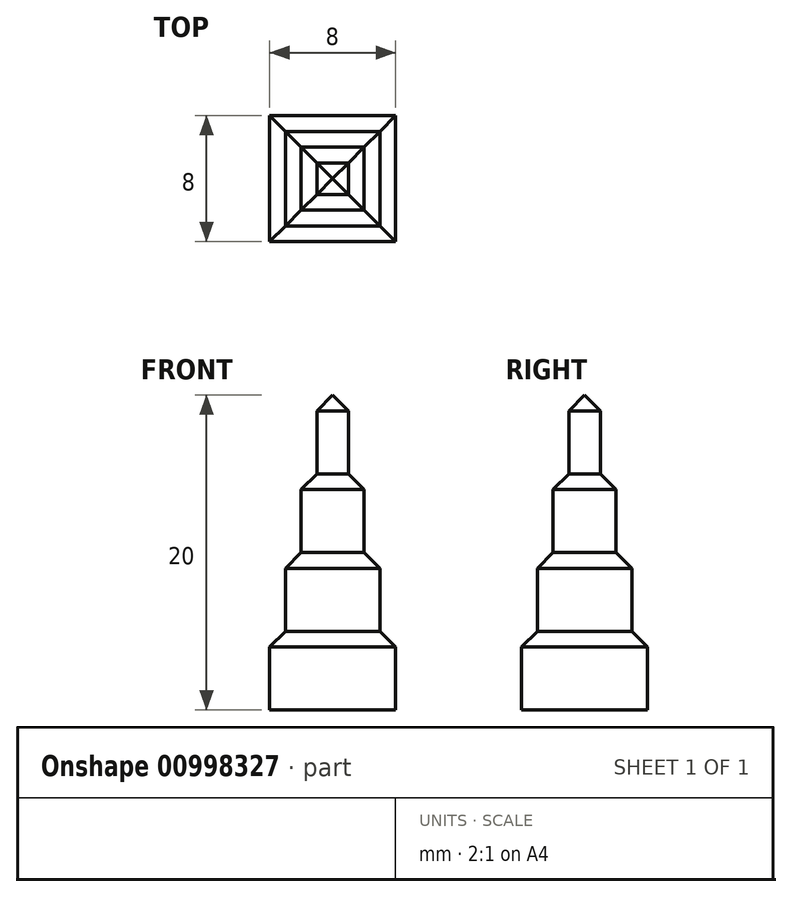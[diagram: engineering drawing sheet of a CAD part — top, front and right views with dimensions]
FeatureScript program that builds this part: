
annotation { "Feature Type Name" : "Feature", "Feature Type Description" : "" }
export const myFeature = defineFeature(function(context is Context, id is Id, definition is map)
    precondition{}
    {
        {
            var Q0;
            Q0=qCreatedBy(makeId("Top.planeOp"),FACE);
            var sketch = newSketch(context, id + "F0", { "sketchPlane" : qUnion([Q0])});
            skLineSegment(sketch, "E0.bottom", {"start": v(1, 1) * mm, "end": v(-1, 1) * mm});
            skLineSegment(sketch, "E0.top", {"start": v(1, -1) * mm, "end": v(-1, -1) * mm});
            skLineSegment(sketch, "E0.left", {"start": v(1, 1) * mm, "end": v(1, -1) * mm});
            skLineSegment(sketch, "E0.right", {"start": v(-1, 1) * mm, "end": v(-1, -1) * mm});
            skPoint(sketch, "E0.middle", {"position": v(0, 0) * mm});
            skLineSegment(sketch, "E1.bottom", {"start": v(2, 2) * mm, "end": v(-2, 2) * mm});
            skLineSegment(sketch, "E1.top", {"start": v(2, -2) * mm, "end": v(-2, -2) * mm});
            skLineSegment(sketch, "E1.left", {"start": v(2, 2) * mm, "end": v(2, -2) * mm});
            skLineSegment(sketch, "E1.right", {"start": v(-2, 2) * mm, "end": v(-2, -2) * mm});
            skLineSegment(sketch, "E2.bottom", {"start": v(3, 3) * mm, "end": v(-3, 3) * mm});
            skLineSegment(sketch, "E2.top", {"start": v(3, -3) * mm, "end": v(-3, -3) * mm});
            skLineSegment(sketch, "E2.left", {"start": v(3, 3) * mm, "end": v(3, -3) * mm});
            skLineSegment(sketch, "E2.right", {"start": v(-3, 3) * mm, "end": v(-3, -3) * mm});
            skLineSegment(sketch, "E3.bottom", {"start": v(4, 4) * mm, "end": v(-4, 4) * mm});
            skLineSegment(sketch, "E3.top", {"start": v(4, -4) * mm, "end": v(-4, -4) * mm});
            skLineSegment(sketch, "E3.left", {"start": v(4, 4) * mm, "end": v(4, -4) * mm});
            skLineSegment(sketch, "E3.right", {"start": v(-4, 4) * mm, "end": v(-4, -4) * mm});
            skSolve(sketch);
        }
        {
            var Q0;
            Q0=makeQuery(id+"F0.imprint","IMPRINT",FACE,{"disambiguationData":[TD([[makeQuery(id+"F0.imprint","IMPRINT",EDGE,{"derivedFrom":sQuery(id+"F0.wireOp",EDGE,"E2.bottom")}),-1.0]])]});
            extrude(context, id + "F1", {"entities" : qUnion([Q0]), "depth" : 5 * mm, "offsetDistance" : 25 * mm});
        }
        {
            var Q0;
            Q0=makeQuery(id+"F0.imprint","IMPRINT",FACE,{"disambiguationData":[TD([[makeQuery(id+"F0.imprint","IMPRINT",EDGE,{"derivedFrom":sQuery(id+"F0.wireOp",EDGE,"E1.bottom")}),-1.0]])]});
            extrude(context, id + "F2", {"entities" : qUnion([Q0]), "operationType" : NewBodyOperationType.ADD, "depth" : 10 * mm, "offsetDistance" : 25 * mm});
        }
        {
            var Q0;
            Q0=makeQuery(id+"F0.imprint","IMPRINT",FACE,{"disambiguationData":[TD([[makeQuery(id+"F0.imprint","IMPRINT",EDGE,{"derivedFrom":sQuery(id+"F0.wireOp",EDGE,"E0.bottom")}),-1.0]])]});
            extrude(context, id + "F3", {"entities" : qUnion([Q0]), "operationType" : NewBodyOperationType.ADD, "depth" : 15 * mm, "offsetDistance" : 25 * mm});
        }
        {
            var Q0;
            Q0=makeQuery(id+"F0.imprint","IMPRINT",FACE,{"disambiguationData":[TD([[makeQuery(id+"F0.imprint","IMPRINT",EDGE,{"derivedFrom":sQuery(id+"F0.wireOp",EDGE,"E0.bottom")}),1.0]])]});
            extrude(context, id + "F4", {"entities" : qUnion([Q0]), "operationType" : NewBodyOperationType.ADD, "depth" : 20 * mm, "offsetDistance" : 25 * mm});
        }
        {
            var Q0;
            Q0=makeQuery(id+"F1.opExtrude","CAP_EDGE",EDGE,{"disambiguationData":[OSD([sQuery(id+"F0.wireOp",EDGE,"E3.top")])],"isStart":false});
            var Q1;
            Q1=makeQuery(id+"F1.opExtrude","CAP_EDGE",EDGE,{"disambiguationData":[OSD([sQuery(id+"F0.wireOp",EDGE,"E3.left")])],"isStart":false});
            var Q2;
            Q2=makeQuery(id+"F1.opExtrude","CAP_EDGE",EDGE,{"disambiguationData":[OSD([sQuery(id+"F0.wireOp",EDGE,"E3.bottom")])],"isStart":false});
            var Q3;
            Q3=makeQuery(id+"F1.opExtrude","CAP_EDGE",EDGE,{"disambiguationData":[OSD([sQuery(id+"F0.wireOp",EDGE,"E3.right")])],"isStart":false});
            var Q4;
            Q4=makeQuery(id+"F2.opExtrude","CAP_EDGE",EDGE,{"disambiguationData":[OSD([sQuery(id+"F0.wireOp",EDGE,"E2.top")])],"isStart":false});
            var Q5;
            Q5=makeQuery(id+"F2.opExtrude","CAP_EDGE",EDGE,{"disambiguationData":[OSD([sQuery(id+"F0.wireOp",EDGE,"E2.left")])],"isStart":false});
            var Q6;
            Q6=makeQuery(id+"F2.opExtrude","CAP_EDGE",EDGE,{"disambiguationData":[OSD([sQuery(id+"F0.wireOp",EDGE,"E2.right")])],"isStart":false});
            var Q7;
            Q7=makeQuery(id+"F2.opExtrude","CAP_EDGE",EDGE,{"disambiguationData":[OSD([sQuery(id+"F0.wireOp",EDGE,"E2.bottom")])],"isStart":false});
            var Q8;
            Q8=makeQuery(id+"F3.opExtrude","CAP_EDGE",EDGE,{"disambiguationData":[OSD([sQuery(id+"F0.wireOp",EDGE,"E1.left")])],"isStart":false});
            var Q9;
            Q9=makeQuery(id+"F3.opExtrude","CAP_EDGE",EDGE,{"disambiguationData":[OSD([sQuery(id+"F0.wireOp",EDGE,"E1.top")])],"isStart":false});
            var Q10;
            Q10=makeQuery(id+"F3.opExtrude","CAP_EDGE",EDGE,{"disambiguationData":[OSD([sQuery(id+"F0.wireOp",EDGE,"E1.right")])],"isStart":false});
            var Q11;
            Q11=makeQuery(id+"F3.opExtrude","CAP_EDGE",EDGE,{"disambiguationData":[OSD([sQuery(id+"F0.wireOp",EDGE,"E1.bottom")])],"isStart":false});
            var Q12;
            Q12=makeQuery(id+"F4.opExtrude","CAP_EDGE",EDGE,{"disambiguationData":[OSD([sQuery(id+"F0.wireOp",EDGE,"E0.left")])],"isStart":false});
            var Q13;
            Q13=makeQuery(id+"F4.opExtrude","CAP_EDGE",EDGE,{"disambiguationData":[OSD([sQuery(id+"F0.wireOp",EDGE,"E0.top")])],"isStart":false});
            var Q14;
            Q14=makeQuery(id+"F4.opExtrude","CAP_EDGE",EDGE,{"disambiguationData":[OSD([sQuery(id+"F0.wireOp",EDGE,"E0.right")])],"isStart":false});
            var Q15;
            Q15=makeQuery(id+"F4.opExtrude","CAP_EDGE",EDGE,{"disambiguationData":[OSD([sQuery(id+"F0.wireOp",EDGE,"E0.bottom")])],"isStart":false});
            chamfer(context, id + "F5", {"entities" : qUnion([Q0, Q1, Q2, Q3, Q4, Q5, Q6, Q7, Q8, Q9, Q10, Q11, Q12, Q13, Q14, Q15]), "width" : 1 * mm, "tangentPropagation" : true});
        }
    });
